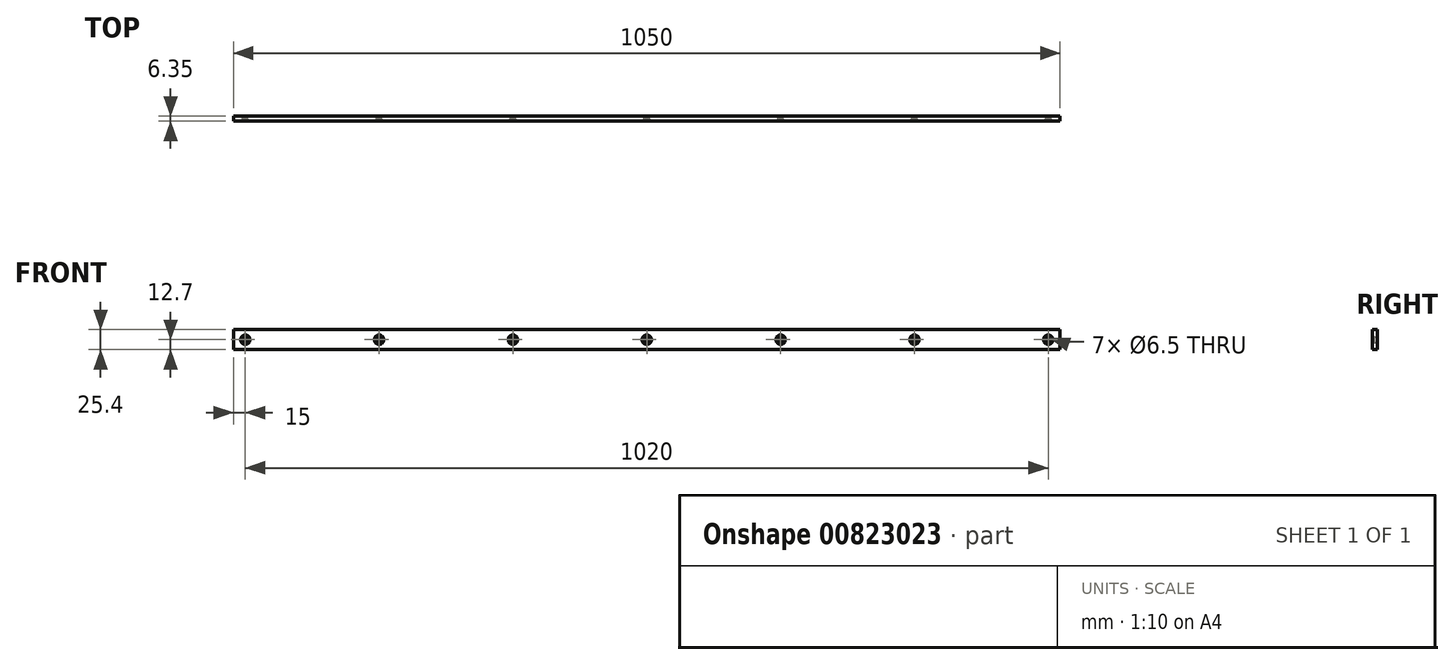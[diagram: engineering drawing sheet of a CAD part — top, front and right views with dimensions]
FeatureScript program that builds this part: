
annotation { "Feature Type Name" : "Feature", "Feature Type Description" : "" }
export const myFeature = defineFeature(function(context is Context, id is Id, definition is map)
    precondition{}
    {
        {
            var Q0;
            Q0=qCreatedBy(makeId("Front.planeOp"),FACE);
            var sketch = newSketch(context, id + "F0", { "sketchPlane" : qUnion([Q0])});
            skLineSegment(sketch, "E0.bottom", {"start": v(525, -12.7) * mm, "end": v(-525, -12.7) * mm});
            skLineSegment(sketch, "E0.top", {"start": v(525, 12.7) * mm, "end": v(-525, 12.7) * mm});
            skLineSegment(sketch, "E0.left", {"start": v(525, -12.7) * mm, "end": v(525, 12.7) * mm});
            skLineSegment(sketch, "E0.right", {"start": v(-525, -12.7) * mm, "end": v(-525, 12.7) * mm});
            skPoint(sketch, "E0.middle", {"position": v(0, 0) * mm});
            skLineSegment(sketch, "E1", {"start": v(0, 0) * mm, "end": v(0, -342.54) * mm, "construction": true});
            skLineSegment(sketch, "E2", {"start": v(0, 0) * mm, "end": v(-510, 0) * mm, "construction": true});
            skLineSegment(sketch, "E3", {"start": v(-510, 0) * mm, "end": v(-510, 337.75) * mm, "construction": true});
            skLineSegment(sketch, "E4", {"start": v(-510, 337.75) * mm, "end": v(-170, 337.75) * mm, "construction": true});
            skLineSegment(sketch, "E5", {"start": v(-170, 337.75) * mm, "end": v(-170, 0) * mm, "construction": true});
            skCircle(sketch, "E6", {"center": v(-510, 0) * mm, "radius": 3.25 * mm});
            skCircle(sketch, "E7", {"center": v(0, 0) * mm, "radius": 3.25 * mm, "construction": true});
            skCircle(sketch, "E8.1.0.0", {"center": v(-340, 0) * mm, "radius": 3.25 * mm});
            skCircle(sketch, "E8.2.0.0", {"center": v(-170, 0) * mm, "radius": 3.25 * mm});
            skCircle(sketch, "E8.3.0.0", {"center": v(0, 0) * mm, "radius": 3.25 * mm});
            skCircle(sketch, "E8.4.0.0", {"center": v(170, 0) * mm, "radius": 3.25 * mm});
            skCircle(sketch, "E8.5.0.0", {"center": v(340, 0) * mm, "radius": 3.25 * mm});
            skCircle(sketch, "E8.6.0.0", {"center": v(510, 0) * mm, "radius": 3.25 * mm});
            skLineSegment(sketch, "E8.direction1", {"start": v(-510, 0) * mm, "end": v(-340, 0) * mm, "construction": true});
            skSolve(sketch);
        }
        {
            var Q0;
            Q0=qSketchRegion(id+"F0",true);
            extrude(context, id + "F1", {"entities" : qUnion([Q0]), "depth" : 6.35 * mm, "offsetDistance" : 25 * mm});
        }
        {
            var Q0;
            Q0=makeQuery(id+"F1.opExtrude","CAP_EDGE",EDGE,{"disambiguationData":[OSD([sQuery(id+"F0.wireOp",EDGE,"E6")])],"isStart":false});
            var Q1;
            Q1=makeQuery(id+"F1.opExtrude","CAP_EDGE",EDGE,{"disambiguationData":[OSD([sQuery(id+"F0.wireOp",EDGE,"E8.2.0.0")])],"isStart":false});
            var Q2;
            Q2=makeQuery(id+"F1.opExtrude","CAP_EDGE",EDGE,{"disambiguationData":[OSD([sQuery(id+"F0.wireOp",EDGE,"E8.1.0.0")])],"isStart":false});
            var Q3;
            Q3=makeQuery(id+"F1.opExtrude","CAP_EDGE",EDGE,{"disambiguationData":[OSD([sQuery(id+"F0.wireOp",EDGE,"E8.3.0.0")])],"isStart":false});
            var Q4;
            Q4=makeQuery(id+"F1.opExtrude","CAP_EDGE",EDGE,{"disambiguationData":[OSD([sQuery(id+"F0.wireOp",EDGE,"E8.4.0.0")])],"isStart":false});
            var Q5;
            Q5=makeQuery(id+"F1.opExtrude","CAP_EDGE",EDGE,{"disambiguationData":[OSD([sQuery(id+"F0.wireOp",EDGE,"E8.6.0.0")])],"isStart":false});
            var Q6;
            Q6=makeQuery(id+"F1.opExtrude","CAP_EDGE",EDGE,{"disambiguationData":[OSD([sQuery(id+"F0.wireOp",EDGE,"E8.5.0.0")])],"isStart":false});
            chamfer(context, id + "F2", {"entities" : qUnion([Q0, Q1, Q2, Q3, Q4, Q5, Q6]), "width" : 2.75 * mm, "tangentPropagation" : true});
        }
        {
            var Q0;
            Q0=makeQuery(id+"F1.opExtrude","CAP_EDGE",EDGE,{"disambiguationData":[OSD([sQuery(id+"F0.wireOp",EDGE,"E6")])],"isStart":true});
            var Q1;
            Q1=makeQuery(id+"F1.opExtrude","CAP_EDGE",EDGE,{"disambiguationData":[OSD([sQuery(id+"F0.wireOp",EDGE,"E8.1.0.0")])],"isStart":true});
            var Q2;
            Q2=makeQuery(id+"F1.opExtrude","CAP_EDGE",EDGE,{"disambiguationData":[OSD([sQuery(id+"F0.wireOp",EDGE,"E8.2.0.0")])],"isStart":true});
            var Q3;
            Q3=makeQuery(id+"F1.opExtrude","CAP_EDGE",EDGE,{"disambiguationData":[OSD([sQuery(id+"F0.wireOp",EDGE,"E8.3.0.0")])],"isStart":true});
            var Q4;
            Q4=makeQuery(id+"F1.opExtrude","CAP_EDGE",EDGE,{"disambiguationData":[OSD([sQuery(id+"F0.wireOp",EDGE,"E8.4.0.0")])],"isStart":true});
            var Q5;
            Q5=makeQuery(id+"F1.opExtrude","CAP_EDGE",EDGE,{"disambiguationData":[OSD([sQuery(id+"F0.wireOp",EDGE,"E8.5.0.0")])],"isStart":true});
            var Q6;
            Q6=makeQuery(id+"F1.opExtrude","CAP_EDGE",EDGE,{"disambiguationData":[OSD([sQuery(id+"F0.wireOp",EDGE,"E8.6.0.0")])],"isStart":true});
            chamfer(context, id + "F3", {"entities" : qUnion([Q0, Q1, Q2, Q3, Q4, Q5, Q6]), "width" : 0.5 * mm, "tangentPropagation" : true});
        }
    });
